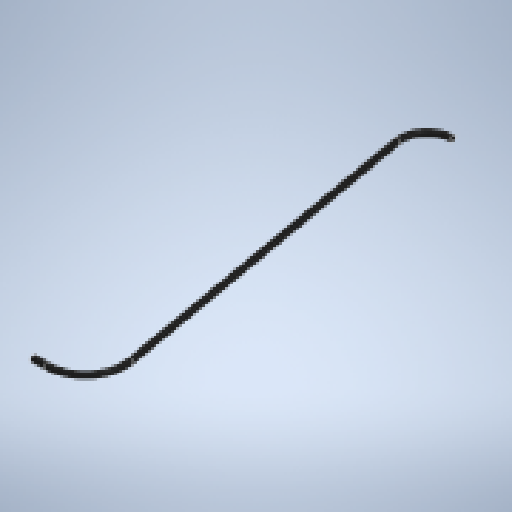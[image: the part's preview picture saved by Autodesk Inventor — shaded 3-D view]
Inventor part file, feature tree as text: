
AUTODESK INVENTOR PART (.ipt)
format: ipt  version: 2025.2 (Build 292293000, 293)  size: 275,968 bytes
history: native  units: mm
features: sketch x4, extrude x2, revolve x2, other x1
ambient origin geometry x8: Origin, YZ Plane, XZ Plane, XY Plane, X Axis, Y Axis, Z Axis, Center Point
bodies: Body1 (feature_tree)
feature tree (9):
  other  "ソリッド1"
  extrude  "押し出し1"  Depth=0.5mm
  revolve  "回転1"
  extrude  "押し出し2"  Depth=1.0mm TaperAngle=0.0deg
  revolve  "回転2"
  sketch  "スケッチ1"
  sketch  "スケッチ2"
  sketch  "スケッチ3"
  sketch  "スケッチ4"
